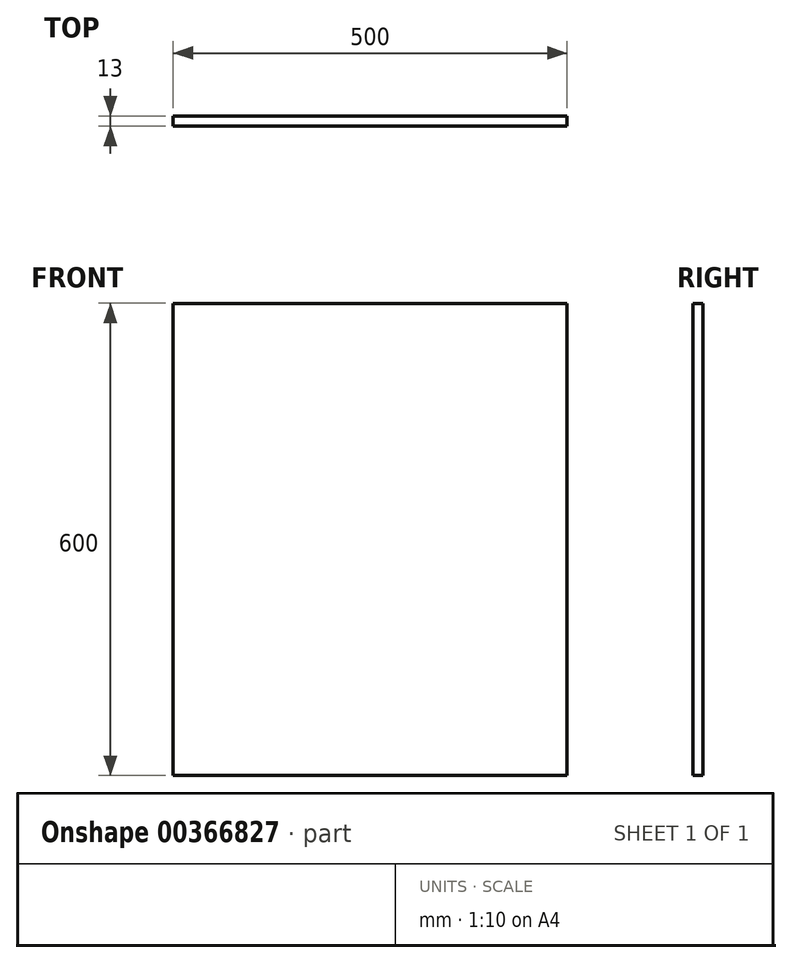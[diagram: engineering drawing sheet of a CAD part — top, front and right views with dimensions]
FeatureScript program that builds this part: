
annotation { "Feature Type Name" : "Feature", "Feature Type Description" : "" }
export const myFeature = defineFeature(function(context is Context, id is Id, definition is map)
    precondition{}
    {
        {
            var Q0;
            Q0=qCreatedBy(makeId("Front.planeOp"),FACE);
            var sketch = newSketch(context, id + "F0", { "sketchPlane" : qUnion([Q0])});
            skLineSegment(sketch, "E0.bottom", {"start": v(-444.18, 551.14) * mm, "end": v(55.82, 551.14) * mm});
            skLineSegment(sketch, "E0.top", {"start": v(-444.18, -48.86) * mm, "end": v(55.82, -48.86) * mm});
            skLineSegment(sketch, "E0.left", {"start": v(-444.18, 551.14) * mm, "end": v(-444.18, -48.86) * mm});
            skLineSegment(sketch, "E0.right", {"start": v(55.82, 551.14) * mm, "end": v(55.82, -48.86) * mm});
            skSolve(sketch);
        }
        {
            var Q0;
            Q0 = qSketchRegion(id + "F0", true);
            extrude(context, id + "F1", {"entities" : qUnion([Q0]), "depth" : 13 * mm});
        }
    });
